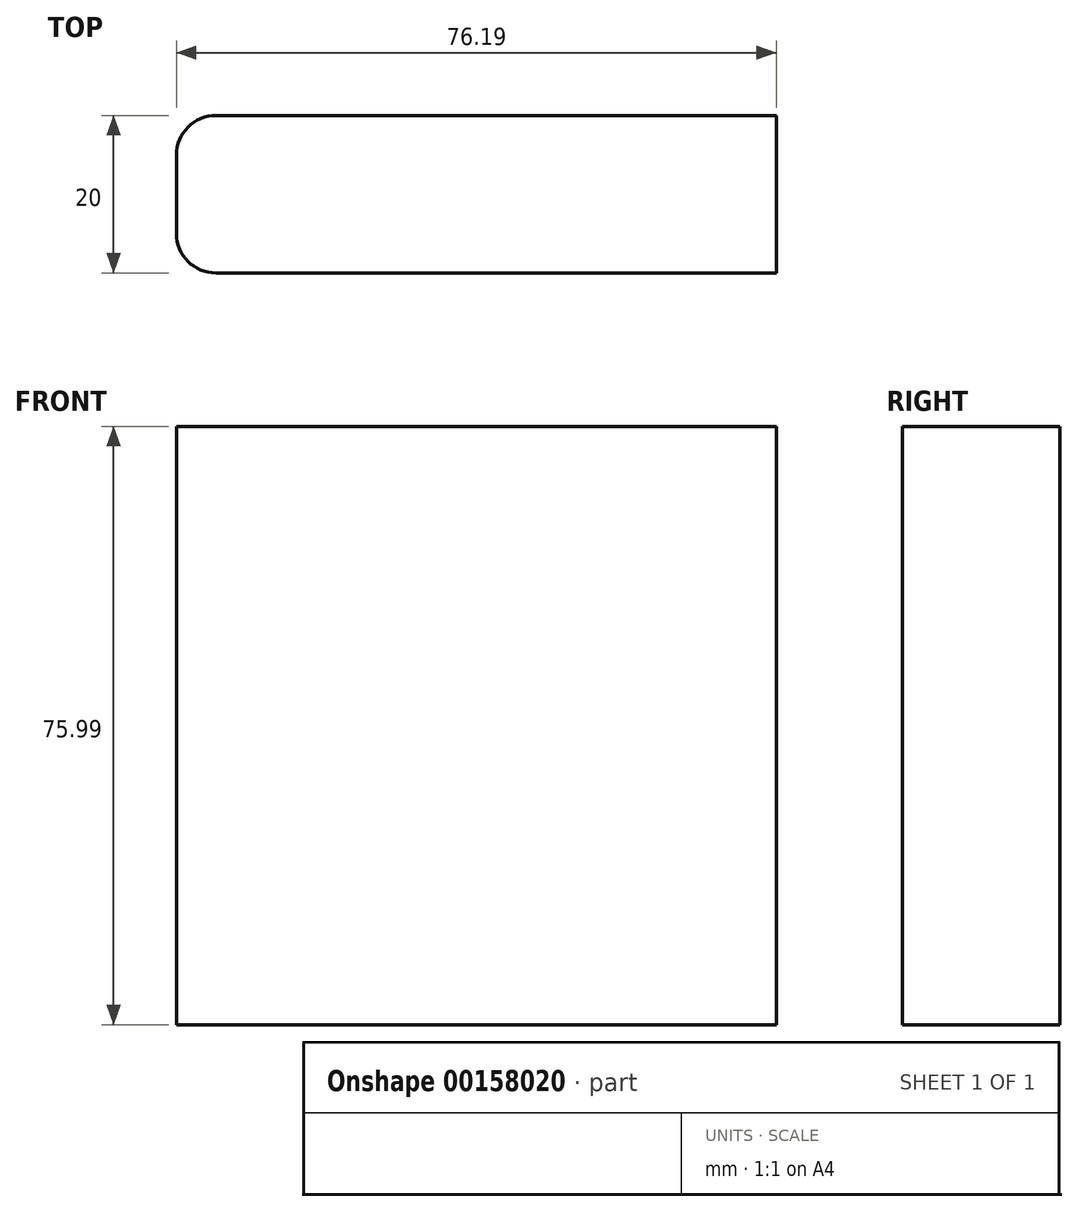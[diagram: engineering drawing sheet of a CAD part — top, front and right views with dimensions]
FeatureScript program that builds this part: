
annotation { "Feature Type Name" : "Feature", "Feature Type Description" : "" }
export const myFeature = defineFeature(function(context is Context, id is Id, definition is map)
    precondition{}
    {
        {
            var Q0;
            Q0=qCreatedBy(makeId("Front.planeOp"),FACE);
            var sketch = newSketch(context, id + "F0", { "sketchPlane" : qUnion([Q0])});
            skLineSegment(sketch, "E0.bottom", {"start": v(0, 75.99) * mm, "end": v(76.2, 75.99) * mm});
            skLineSegment(sketch, "E0.top", {"start": v(0, 0) * mm, "end": v(76.2, 0) * mm});
            skLineSegment(sketch, "E0.left", {"start": v(0, 75.99) * mm, "end": v(0, 0) * mm});
            skLineSegment(sketch, "E0.right", {"start": v(76.2, 75.99) * mm, "end": v(76.2, 0) * mm});
            skSolve(sketch);
        }
        {
            var Q0;
            Q0 = qSketchRegion(id + "F0", true);
            extrude(context, id + "F1", {"entities" : qUnion([Q0]), "depth" : 20 * mm});
        }
        {
            var Q0;
            Q0=makeQuery(id+"F1.opExtrude","CAP_FACE",FACE,{"disambiguationData":[OSD([sQuery(id+"F0.wireOp",EDGE,"E0.bottom"),sQuery(id+"F0.wireOp",EDGE,"E0.top"),sQuery(id+"F0.wireOp",EDGE,"E0.left"),sQuery(id+"F0.wireOp",EDGE,"E0.right")])],"isStart":false});
            var sketch = newSketch(context, id + "F2", { "sketchPlane" : qUnion([Q0])});
            skCircle(sketch, "E1", {"center": v(39, 38.14) * mm, "radius": 14 * mm});
            skSolve(sketch);
        }
        {
            var Q0;
            Q0=sQuery(id+"F2.wireOp",EDGE,"E1");
            extrude(context, id + "F3", {"bodyType" : ToolBodyType.SURFACE, "surfaceEntities" : qUnion([Q0]), "depth" : 25 * mm});
        }
        {
            var Q0;
            Q0=makeQuery(id+"F1.opExtrude","CAP_EDGE",EDGE,{"disambiguationData":[OSD([sQuery(id+"F0.wireOp",EDGE,"E0.left")])],"isStart":false});
            var Q1;
            Q1=makeQuery(id+"F1.opExtrude","CAP_EDGE",EDGE,{"disambiguationData":[OSD([sQuery(id+"F0.wireOp",EDGE,"E0.left")])],"isStart":true});
            fillet(context, id + "F4", {"entities" : qUnion([Q0, Q1]), "radius" : 5 * mm, "tangentPropagation" : true, "allowEdgeOverflow" : false});
        }
    });
